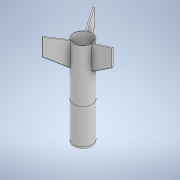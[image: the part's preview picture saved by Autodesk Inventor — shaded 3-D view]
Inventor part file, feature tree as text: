
AUTODESK INVENTOR PART (.ipt)
format: ipt  version: 2020.3 (Build 243373000, 373)  size: 274,944 bytes
history: native  units: mm
features: extrude x6, sketch x5, plane x2, chamfer x2, projected_geometry x2, pattern_circular x1, split x1
ambient origin geometry x8: Origin, YZ Plane, XZ Plane, XY Plane, X Axis, Y Axis, Z Axis, Center Point
bodies: Solid1 (feature_tree), Solid2 (feature_tree), Solid3 (feature_tree)
feature tree (19):
  sketch  "Sketch1"  dims[d0=50.0mm d1=51.8mm]
  extrude  "Extrusion1"  Depth=51.8mm
  extrude  "Extrusion2"  Depth=75.0mm TaperAngle=0.0deg
  extrude  "Extrusion4"  Depth=70.0mm
  plane  "Work Plane1"
  extrude  "Extrusion5"  Depth=50.0mm
  chamfer  "Chamfer1"  Distance=3.6mm
  chamfer  "Chamfer2"  Distance=175.0mm
  pattern_circular  "Circular Pattern3"  [2 undecoded]
  plane  "Work Plane2"
  split  "Split1"
  extrude  "Extrusion6"  [1 undecoded]
  extrude  "Extrusion7"  Depth=5.0mm TaperAngle=45.0deg
  sketch  "Sketch4"  dims[d2=53.6mm d3=75.0mm d4=180.0mm d5=0.0mm d6=0.0mm]
  projected_geometry  "Projected Loop1"
  sketch  "Sketch7"  dims[d21=9.930923mm d24=50.0mm]
  sketch  "Sketch8"  dims[d25=60.0mm d26=3.6mm d27=0.0mm d31=175.0mm d32=0.0mm d33=5.0mm d34=-145.0mm d35=50.0mm d36=51.8mm d37=53.6mm d38=5.0mm d39=5.0mm d40=0.0mm d41=1.8mm d42=2.0mm d43=45.0deg d44=1.8mm d45=2.0mm d46=45.0deg d47=30.0mm d48=360.0deg d50=-75.0mm d51=50.0mm d52=51.8mm d53=5.0mm d54=0.0mm d55=50.0mm d56=51.8mm d57=5.0mm d58=0.0mm d11=0.5mm d12=0.872665mm d13=0.5mm d14=0.872665mm]
  projected_geometry  "Project Cut Edges1"
  sketch  "Sketch5"  dims[d7=75.0mm d8=0.0mm d18=70.0mm]
note: 3 required parameter values undecoded (feature->parameter linkage not recoverable at this tier; creation-order binding heuristic only, values carry confidence <= 0.55)
